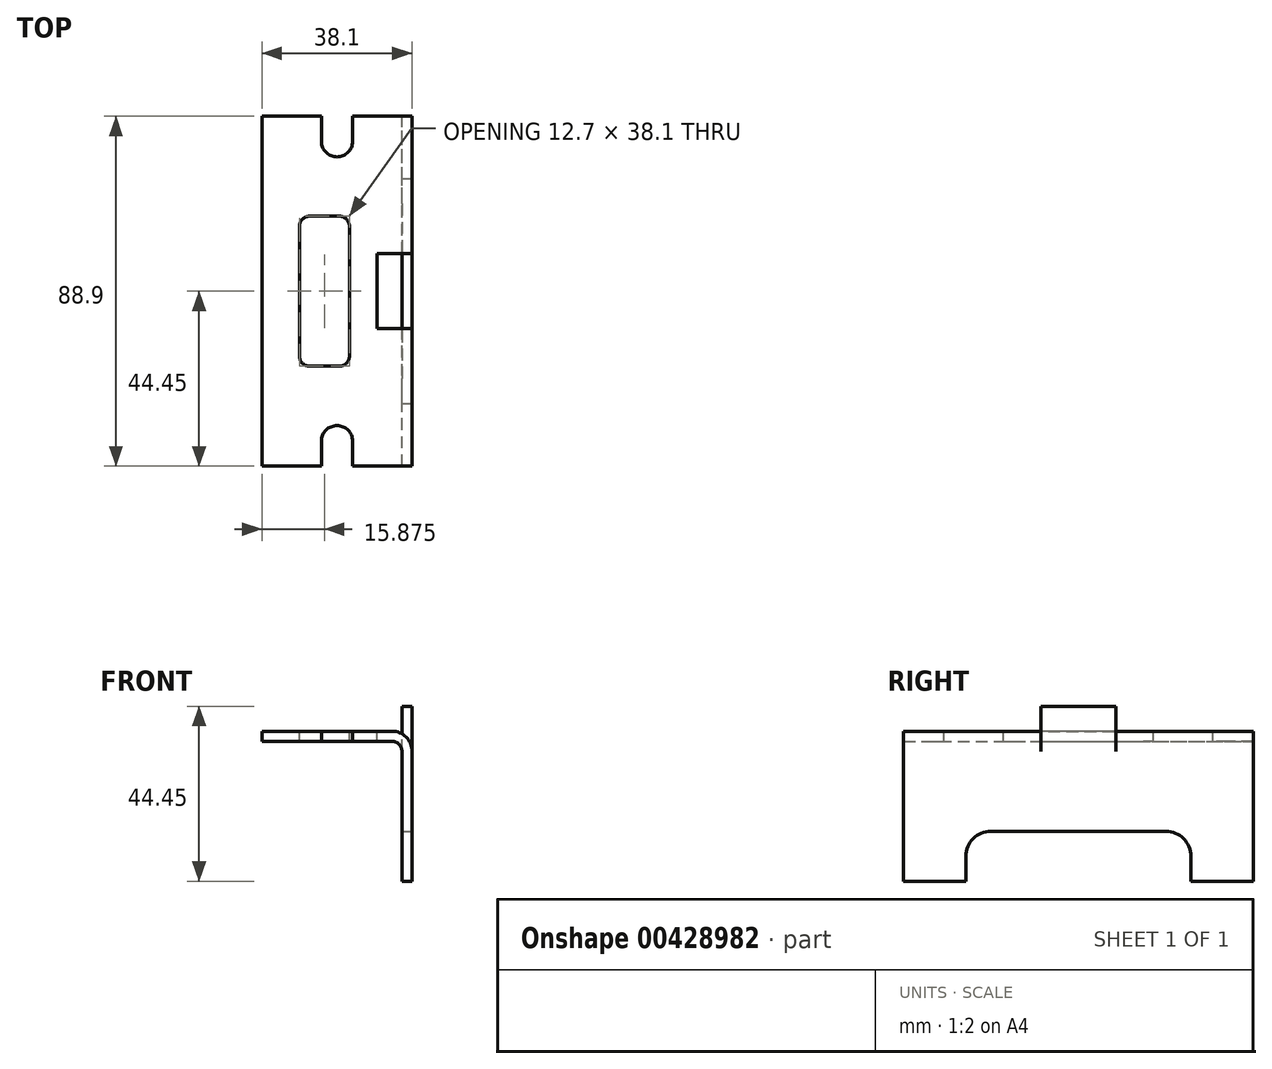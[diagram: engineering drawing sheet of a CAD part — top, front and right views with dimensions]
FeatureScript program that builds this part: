
annotation { "Feature Type Name" : "Feature", "Feature Type Description" : "" }
export const myFeature = defineFeature(function(context is Context, id is Id, definition is map)
    precondition{}
    {
        {
            var Q0;
            Q0=qCreatedBy(makeId("Front.planeOp"),FACE);
            var sketch = newSketch(context, id + "F0", { "sketchPlane" : qUnion([Q0])});
            skLineSegment(sketch, "E0", {"start": v(-5.08, 0) * mm, "end": v(-38.1, 0) * mm});
            skLineSegment(sketch, "E1", {"start": v(0, -38.1) * mm, "end": v(-2.54, -38.1) * mm});
            skLineSegment(sketch, "E2", {"start": v(-2.54, -38.1) * mm, "end": v(-2.54, -5.08) * mm});
            skLineSegment(sketch, "E3", {"start": v(-5.08, -2.54) * mm, "end": v(-38.1, -2.54) * mm});
            skLineSegment(sketch, "E4", {"start": v(-38.1, -2.54) * mm, "end": v(-38.1, 0) * mm});
            skPoint(sketch, "E5.visualSharp", {"position": v(-2.54, -2.54) * mm});
            skArc(sketch, "E5.filletArc", {"start": v(-2.54, -5.08) * mm, "mid": v(-3.28, -3.28) * mm, "end": v(-5.08, -2.54) * mm});
            skLineSegment(sketch, "E6", {"start": v(0, -38.1) * mm, "end": v(0, -3.75) * mm});
            skArc(sketch, "E7.0", {"start": v(0, -5.08) * mm, "mid": v(-1.49, -1.49) * mm, "end": v(-5.08, 0) * mm});
            skPoint(sketch, "E8.orphan", {"position": v(0, 0) * mm});
            skSolve(sketch);
        }
        {
            var Q0;
            Q0=qSketchRegion(id+"F0",true);
            extrude(context, id + "F1", {"entities" : qUnion([Q0]), "depth" : 88.9 * mm});
        }
        {
            var Q0;
            Q0=makeQuery(id+"F1.opExtrude","SWEPT_FACE",FACE,{"disambiguationData":[OSD([sQuery(id+"F0.wireOp",EDGE,"E0")])]});
            var sketch = newSketch(context, id + "F2", { "sketchPlane" : qUnion([Q0])});
            skLineSegment(sketch, "E9.bottom", {"start": v(-2.54, -34.93) * mm, "end": v(-8.9, -34.93) * mm});
            skLineSegment(sketch, "E9.top", {"start": v(-2.54, -53.98) * mm, "end": v(-8.9, -53.98) * mm});
            skLineSegment(sketch, "E9.left", {"start": v(-2.54, -34.93) * mm, "end": v(-2.54, -53.98) * mm});
            skLineSegment(sketch, "E9.right", {"start": v(-8.9, -34.93) * mm, "end": v(-8.9, -53.98) * mm});
            skPoint(sketch, "E10.bottom.start.orphan", {"position": v(-21.59, -88.9) * mm});
            skPoint(sketch, "E10.top.end.orphan", {"position": v(-5.72, -53.98) * mm});
            skSolve(sketch);
        }
        {
            var Q0;
            Q0=makeQuery(id+"F2.imprint","IMPRINT",FACE,{"disambiguationData":[TD([[makeQuery(id+"F2.imprint","IMPRINT",EDGE,{"derivedFrom":sQuery(id+"F2.wireOp",EDGE,"E9.bottom")}),1.0]])]});
            extrude(context, id + "F3", {"entities" : qUnion([Q0]), "operationType" : NewBodyOperationType.REMOVE, "oppositeDirection" : true, "depth" : 25.4 * mm});
        }
        {
            var Q0;
            Q0=makeQuery(id+"F1.opExtrude","SWEPT_FACE",FACE,{"disambiguationData":[OSD([sQuery(id+"F0.wireOp",EDGE,"E0")])]});
            var sketch = newSketch(context, id + "F4", { "sketchPlane" : qUnion([Q0])});
            skLineSegment(sketch, "E11.bottom", {"start": v(-2.54, -34.93) * mm, "end": v(0, -34.93) * mm});
            skLineSegment(sketch, "E11.top", {"start": v(-2.54, -53.98) * mm, "end": v(0, -53.98) * mm});
            skLineSegment(sketch, "E11.left", {"start": v(-2.54, -34.93) * mm, "end": v(-2.54, -53.98) * mm});
            skLineSegment(sketch, "E11.right", {"start": v(0, -34.93) * mm, "end": v(0, -53.98) * mm});
            skSolve(sketch);
        }
        {
            var Q0;
            Q0=qSketchRegion(id+"F4",true);
            extrude(context, id + "F5", {"entities" : qUnion([Q0]), "operationType" : NewBodyOperationType.ADD, "depth" : 6.35 * mm, "hasSecondDirection" : true, "secondDirectionOppositeDirection" : true, "secondDirectionDepth" : 6.35 * mm});
        }
        {
            var Q0;
            {var subQ0=sQuery(id+"F2.wireOp",EDGE,"E9.right");Q0=makeQuery(id+"F2.imprint","IMPRINT",FACE,{"disambiguationData":[TD([[makeQuery(id+"F2.imprint","IMPRINT",EDGE,{"derivedFrom":subQ0}),-1.0]])]});}
            var sketch = newSketch(context, id + "F6", { "sketchPlane" : qUnion([Q0])});
            skArc(sketch, "E12", {"start": v(-23.02, -6.35) * mm, "mid": v(-19.05, -10.32) * mm, "end": v(-15.08, -6.35) * mm});
            skArc(sketch, "E13", {"start": v(-15.08, -82.55) * mm, "mid": v(-19.05, -78.58) * mm, "end": v(-23.02, -82.55) * mm});
            skLineSegment(sketch, "E14", {"start": v(-23.02, -6.35) * mm, "end": v(-23.02, 0) * mm});
            skLineSegment(sketch, "E15", {"start": v(-15.08, -6.35) * mm, "end": v(-15.08, 0) * mm});
            skPoint(sketch, "E16.start.orphan", {"position": v(-19.05, 0) * mm});
            skLineSegment(sketch, "E17", {"start": v(-23.02, 0) * mm, "end": v(-15.08, 0) * mm});
            skLineSegment(sketch, "E18", {"start": v(-15.08, -82.55) * mm, "end": v(-15.08, -89) * mm});
            skLineSegment(sketch, "E19", {"start": v(-23.02, -82.55) * mm, "end": v(-23.02, -89) * mm});
            skLineSegment(sketch, "E20", {"start": v(-23.02, -89) * mm, "end": v(-15.08, -89) * mm});
            skSolve(sketch);
        }
        {
            var Q0;
            Q0=qSketchRegion(id+"F6",true);
            extrude(context, id + "F7", {"entities" : qUnion([Q0]), "operationType" : NewBodyOperationType.REMOVE, "oppositeDirection" : true, "depth" : 25.4 * mm});
        }
        {
            var Q0;
            {var subQ0=sQuery(id+"F2.wireOp",EDGE,"E9.right");Q0=makeQuery(id+"F2.imprint","IMPRINT",FACE,{"disambiguationData":[TD([[makeQuery(id+"F2.imprint","IMPRINT",EDGE,{"derivedFrom":subQ0}),-1.0]])]});}
            var sketch = newSketch(context, id + "F8", { "sketchPlane" : qUnion([Q0])});
            skLineSegment(sketch, "E21.bottom", {"start": v(-26.04, -25.4) * mm, "end": v(-18.42, -25.4) * mm});
            skLineSegment(sketch, "E21.top", {"start": v(-26.03, -63.5) * mm, "end": v(-18.41, -63.5) * mm});
            skLineSegment(sketch, "E21.left", {"start": v(-28.58, -27.94) * mm, "end": v(-28.57, -60.96) * mm});
            skLineSegment(sketch, "E21.right", {"start": v(-15.88, -27.94) * mm, "end": v(-15.87, -60.96) * mm});
            skPoint(sketch, "E22.visualSharp", {"position": v(-28.58, -25.4) * mm});
            skArc(sketch, "E22.filletArc", {"start": v(-26.04, -25.4) * mm, "mid": v(-27.83, -26.14) * mm, "end": v(-28.58, -27.94) * mm});
            skPoint(sketch, "E23.visualSharp", {"position": v(-15.88, -25.4) * mm});
            skArc(sketch, "E23.filletArc", {"start": v(-15.88, -27.94) * mm, "mid": v(-16.62, -26.14) * mm, "end": v(-18.42, -25.4) * mm});
            skPoint(sketch, "E24.visualSharp", {"position": v(-28.57, -63.5) * mm});
            skArc(sketch, "E24.filletArc", {"start": v(-28.57, -60.96) * mm, "mid": v(-27.83, -62.76) * mm, "end": v(-26.03, -63.5) * mm});
            skPoint(sketch, "E25.visualSharp", {"position": v(-15.87, -63.5) * mm});
            skArc(sketch, "E25.filletArc", {"start": v(-18.41, -63.5) * mm, "mid": v(-16.62, -62.76) * mm, "end": v(-15.88, -60.96) * mm});
            skSolve(sketch);
        }
        {
            var Q0;
            Q0=qSketchRegion(id+"F8",true);
            extrude(context, id + "F9", {"entities" : qUnion([Q0]), "operationType" : NewBodyOperationType.REMOVE, "oppositeDirection" : true, "depth" : 25.4 * mm});
        }
        {
            var Q0;
            Q0=makeQuery(id+"F5.boolean.opBoolean","MERGE",FACE,{"derivedFrom":[makeQuery(id+"F1.opExtrude","SWEPT_FACE",FACE,{"disambiguationData":[OSD([sQuery(id+"F0.wireOp",EDGE,"E6")])]}),makeQuery(id+"F5.opExtrude","SWEPT_FACE",FACE,{"disambiguationData":[OSD([sQuery(id+"F4.wireOp",EDGE,"E11.right")])]})]});
            var sketch = newSketch(context, id + "F10", { "sketchPlane" : qUnion([Q0])});
            skLineSegment(sketch, "E26.bottom", {"start": v(-73.03, -38.1) * mm, "end": v(-15.88, -38.1) * mm});
            skLineSegment(sketch, "E26.top", {"start": v(-66.68, -25.4) * mm, "end": v(-22.23, -25.4) * mm});
            skLineSegment(sketch, "E26.left", {"start": v(-73.03, -38.1) * mm, "end": v(-73.03, -31.75) * mm});
            skLineSegment(sketch, "E26.right", {"start": v(-15.88, -38.1) * mm, "end": v(-15.88, -31.75) * mm});
            skPoint(sketch, "E27.visualSharp", {"position": v(-73.03, -25.4) * mm});
            skArc(sketch, "E27.filletArc", {"start": v(-66.68, -25.4) * mm, "mid": v(-71.17, -27.26) * mm, "end": v(-73.03, -31.75) * mm});
            skPoint(sketch, "E28.visualSharp", {"position": v(-15.88, -25.4) * mm});
            skArc(sketch, "E28.filletArc", {"start": v(-15.87, -31.75) * mm, "mid": v(-17.73, -27.26) * mm, "end": v(-22.23, -25.4) * mm});
            skSolve(sketch);
        }
        {
            var Q0;
            Q0=qSketchRegion(id+"F10",true);
            extrude(context, id + "F11", {"entities" : qUnion([Q0]), "operationType" : NewBodyOperationType.REMOVE, "oppositeDirection" : true, "depth" : 25.4 * mm});
        }
    });
